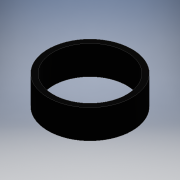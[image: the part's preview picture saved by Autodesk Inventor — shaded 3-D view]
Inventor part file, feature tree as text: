
AUTODESK INVENTOR PART (.ipt)
format: ipt  version: 2016 (Build 200138000, 138)  size: 95,232 bytes
history: native  units: mm
features: other x1, sketch x1, extrude x1
ambient origin geometry x8: Origin, YZ Plane, XZ Plane, XY Plane, X Axis, Y Axis, Z Axis, Center Point
bodies: Body1 (feature_tree)
feature tree (3):
  other  "ソリッド1"
  sketch  "スケッチ1"
  extrude  "押し出し1"  Depth=14.0mm
